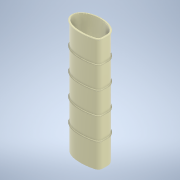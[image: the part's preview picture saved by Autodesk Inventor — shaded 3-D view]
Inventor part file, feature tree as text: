
AUTODESK INVENTOR PART (.ipt)
format: ipt  version: 2022 (Build 260153070, 153G)  size: 530,944 bytes
history: native  units: mm
features: extrude x3, sketch x3, other x2, fillet x2, projected_geometry x2, shell x1, thicken_offset x1, pattern_linear x1
ambient origin geometry x8: Origin, YZ Plane, XZ Plane, XY Plane, X Axis, Y Axis, Z Axis, Center Point
bodies: Solid3 (feature_tree), Solid4 (feature_tree)
feature tree (15):
  extrude  "Extrusion4"  Depth=300.0mm
  shell  "Shell1"  Thickness=21.0mm
  other  "Work Axis1"
  fillet  "Fillet2"  Radius=300.0mm
  extrude  "Extrusion5"  Depth=5.0mm
  other  "Work Point1"
  extrude  "Extrusion6"  Depth=46.0mm
  thicken_offset  "Thicken1"
  fillet  "Fillet3"  Radius=5.0mm
  pattern_linear  "Rectangular Pattern1"  Spacing1=5.0mm  [1 undecoded]
  sketch  "Sketch2"  dims[d9=10.0mm d10=120.0mm d11=21.0mm d12=300.0mm d13=0.0mm]
  sketch  "Sketch6"  dims[d14=2.0mm d16=5.0mm]
  projected_geometry  "Projected Loop1"
  sketch  "Sketch7"  dims[d19=5.0mm d20=5.0mm d21=5.0mm d22=5.0mm d23=5.0mm d24=3.0mm d25=0.0mm d26=28.0mm d27=46.0mm d28=3.0mm d29=0.0mm d30=2.0mm d31=2.0mm d33=1.5mm d34=50.0mm d36=60.0mm]
  projected_geometry  "Projected Loop2"
note: 1 required parameter value undecoded (feature->parameter linkage not recoverable at this tier; creation-order binding heuristic only, values carry confidence <= 0.55)
